# Revit family: IS_IdealSystem_W3708_BIM_NL
name_source: partatom
category: Plumbing Fixtures
revit_build: Autodesk Revit MEP 2014 (Build: 20130308_1515(x64)
units: mm (PartAtom-declared; Revit-internal decimal feet)

## types (1)
- W3708AC - BEDIENINGSPANEEL RECHTHOEKIG 2F WIT
    Accessories = www.idealstandardnederland.nl
    AreaUnits = millimeters
    Assembly Code = C1030200
    AssetType = Vast
    BIMObjectName = ISI_IdealStandard_WcCisternFittings_W3708AC
    BREEAMApproved = No
    BarCode = 3800828021785
    Brand = Ideal Standard
    CWFU = 0
    ConnectionType = Sanitair
    Cost = 0 $
    Default Elevation = 0 mm  [stored 0 ft]
    Description = Drukplaat rechthoekig met rechte hoeken.
    DurationUnit = jaar
    ECA = No
    ExpectedLife = 25
    Features = Drukplaat rechthoekig met rechte hoeken.
    Finish = Wit
    HWFU = 0
    IfcExportAs = IfcSanitaryTerminalType
    IfcExportType = CISTERN
    InstallationInstructions = http://www.idealstandardnederland.nl
    LinearUnits = millimeters
    ManufacturerURL = www.idealstandardnederland.nl
    Model = W3708AC
    ModelNumber = W3708AC
    ModelReference = Drukplaat rechthoekig met rechte hoeken.
    NBSDescription = WC cistern fittings
    NBSReference = 45-30-70/387
    Name = WcCisternFittings_W3708AC_IdealStandard
    NettWeight = 0.44 kg
    NominalDepth = 10 mm  [stored 0.0328084 ft]
    NominalHeight = 170 mm
    NominalLength = 0 mm  [stored 0 ft]
    NominalWidth = 230 mm
    ProductInformation = http://www.idealstandardnederland.nl
    Shape = Rechthoekig
    Size = 230 x 170 x 10mm
    Space = Internal
    SpilloverLevel = 0 mm  [stored 0 ft]
    ToiletPanType = WashDown
    ToiletType = Other
    URL = www.idealstandardnederland.nl
    Uniclass2015Code = Pr_40_20_93_87
    Uniclass2015Title = WC cistern fittings
    Uniclass2015Version = Products v1.1
    Version = 1
    VolumeUnits = liter
    WFU = 0
    WRAS = No
    WarrantyDescription = Fabrieksgarantie
    WarrantyDurationParts = 5
    WarrantyDurationUnit = jaar
    WaterEfficientProduct = No

note: [stored X ft] marks values corroborated as IEEE doubles in the binary element streams (Revit-internal decimal feet)

## geometry (parser evidence)
native form markers: Sweep x1
no freeform markers — native parametric forms only
